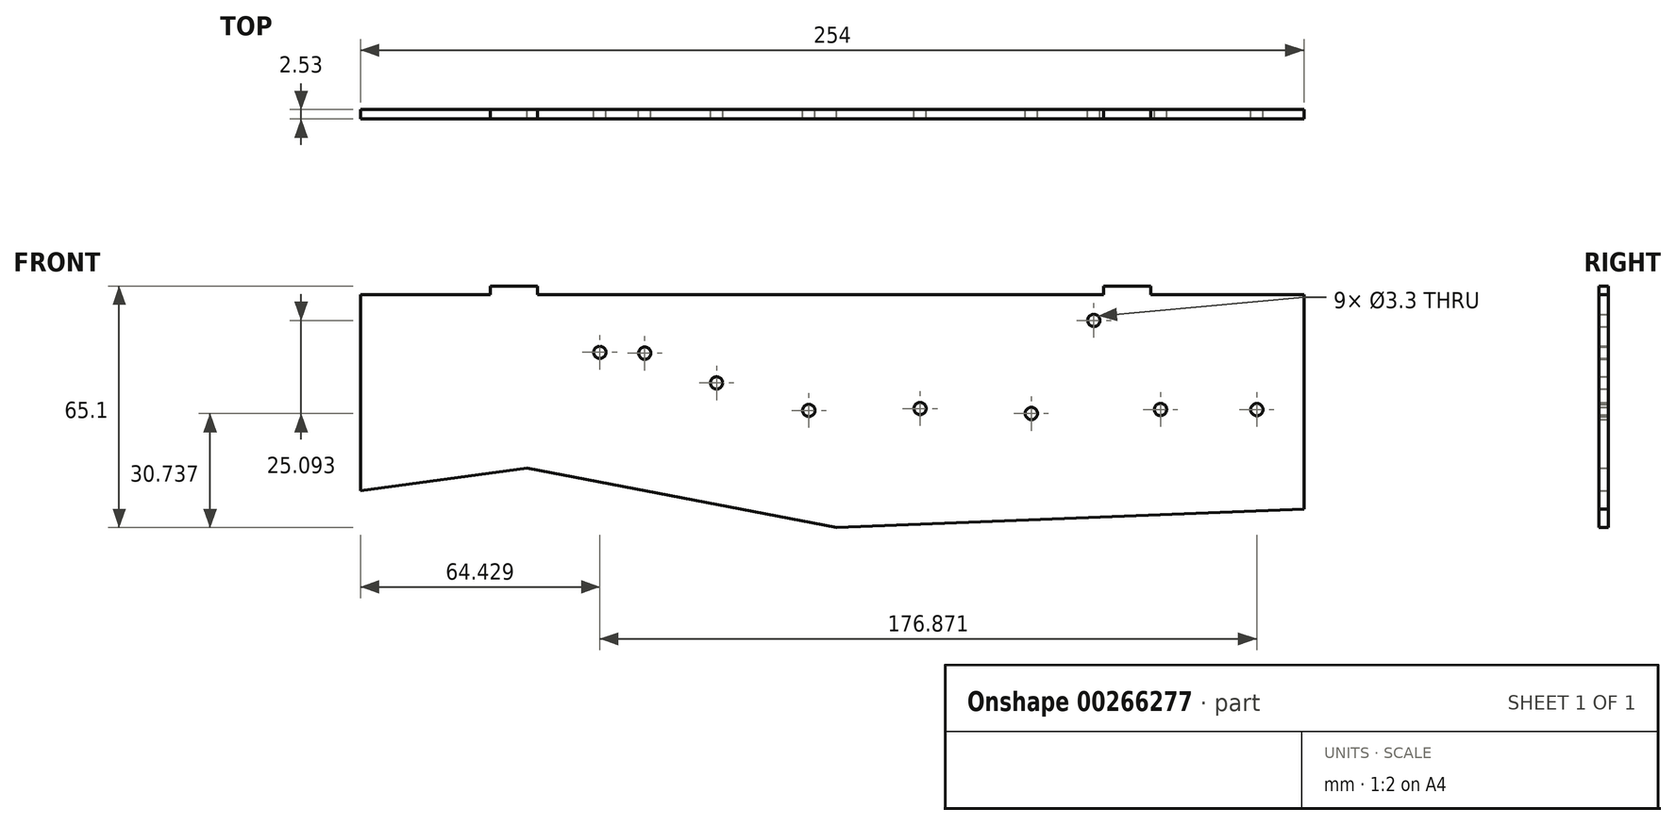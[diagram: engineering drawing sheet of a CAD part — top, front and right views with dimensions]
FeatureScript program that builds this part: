
annotation { "Feature Type Name" : "Feature", "Feature Type Description" : "" }
export const myFeature = defineFeature(function(context is Context, id is Id, definition is map)
    precondition{}
    {
        {
            var Q0;
            Q0=qCreatedBy(makeId("Front.planeOp"),FACE);
            var sketch = newSketch(context, id + "F0", { "sketchPlane" : qUnion([Q0])});
            skLineSegment(sketch, "E0.top", {"start": v(0, 76.2) * mm, "end": v(-254, 76.2) * mm});
            skLineSegment(sketch, "E0.left", {"start": v(0, 0) * mm, "end": v(0, 76.2) * mm});
            skCircle(sketch, "E1", {"center": v(-12.7, 45.18) * mm, "radius": 1.65 * mm});
            skCircle(sketch, "E2", {"center": v(-38.63, 45.21) * mm, "radius": 1.65 * mm});
            skCircle(sketch, "E3", {"center": v(-73.4, 44.13) * mm, "radius": 1.65 * mm});
            skCircle(sketch, "E4", {"center": v(-103.35, 45.47) * mm, "radius": 1.65 * mm});
            skCircle(sketch, "E5", {"center": v(-133.3, 44.95) * mm, "radius": 1.65 * mm});
            skCircle(sketch, "E6", {"center": v(-158.15, 52.37) * mm, "radius": 1.65 * mm});
            skCircle(sketch, "E7", {"center": v(-177.48, 60.4) * mm, "radius": 1.65 * mm});
            skLineSegment(sketch, "E8", {"start": v(-254, 76.2) * mm, "end": v(-254, 0) * mm});
            skLineSegment(sketch, "E9", {"start": v(-254, 0) * mm, "end": v(0, 0) * mm});
            skLineSegment(sketch, "E10", {"start": v(0, 18.33) * mm, "end": v(-125.8, 13.39) * mm});
            skLineSegment(sketch, "E11", {"start": v(-125.8, 13.39) * mm, "end": v(-209.2, 29.45) * mm});
            skLineSegment(sketch, "E12", {"start": v(-209.2, 29.45) * mm, "end": v(-254, 23.27) * mm});
            skCircle(sketch, "E13", {"center": v(-189.57, 60.6) * mm, "radius": 1.65 * mm});
            skCircle(sketch, "E14", {"center": v(-56.57, 69.22) * mm, "radius": 1.65 * mm});
            skSolve(sketch);
        }
        {
            var Q0;
            Q0=makeQuery(id+"F0.imprint","IMPRINT",FACE,{"disambiguationData":[TD([[makeQuery(id+"F0.imprint","IMPRINT",EDGE,{"derivedFrom":sQuery(id+"F0.wireOp",EDGE,"E0.top")}),1.0]])]});
            extrude(context, id + "F1", {"entities" : qUnion([Q0]), "depth" : 2.53 * mm});
        }
        {
            var Q0;
            Q0=makeQuery(id+"F1.opExtrude","SWEPT_FACE",FACE,{"disambiguationData":[OSD([sQuery(id+"F0.wireOp",EDGE,"E0.top")])]});
            var sketch = newSketch(context, id + "F2", { "sketchPlane" : qUnion([Q0])});
            skLineSegment(sketch, "E15.bottom", {"start": v(-41.25, 0) * mm, "end": v(-53.95, 0) * mm});
            skLineSegment(sketch, "E15.top", {"start": v(-41.25, -2.53) * mm, "end": v(-53.95, -2.53) * mm});
            skLineSegment(sketch, "E15.left", {"start": v(-41.25, 0) * mm, "end": v(-41.25, -2.53) * mm});
            skLineSegment(sketch, "E15.right", {"start": v(-53.95, 0) * mm, "end": v(-53.95, -2.53) * mm});
            skLineSegment(sketch, "E16.bottom", {"start": v(-206.35, 0) * mm, "end": v(-219.05, 0) * mm});
            skLineSegment(sketch, "E16.top", {"start": v(-206.35, -2.53) * mm, "end": v(-219.05, -2.53) * mm});
            skLineSegment(sketch, "E16.left", {"start": v(-206.35, 0) * mm, "end": v(-206.35, -2.53) * mm});
            skLineSegment(sketch, "E16.right", {"start": v(-219.05, 0) * mm, "end": v(-219.05, -2.53) * mm});
            skSolve(sketch);
        }
        {
            var Q0;
            Q0 = qSketchRegion(id + "F2", true);
            extrude(context, id + "F3", {"entities" : qUnion([Q0]), "operationType" : NewBodyOperationType.ADD, "depth" : 2.3 * mm});
        }
    });
